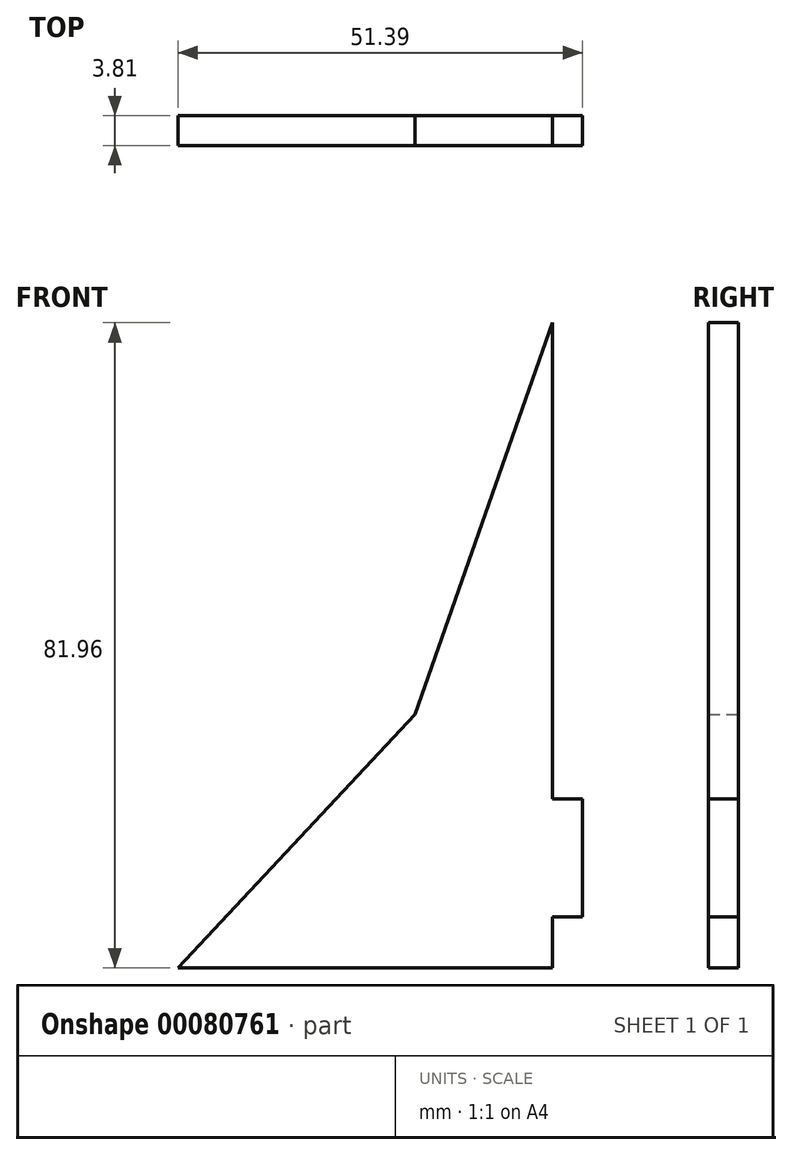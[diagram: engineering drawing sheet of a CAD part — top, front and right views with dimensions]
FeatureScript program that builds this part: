
annotation { "Feature Type Name" : "Feature", "Feature Type Description" : "" }
export const myFeature = defineFeature(function(context is Context, id is Id, definition is map)
    precondition{}
    {
        {
            var Q0;
            Q0=qCreatedBy(makeId("Front.planeOp"),FACE);
            var sketch = newSketch(context, id + "F0", { "sketchPlane" : qUnion([Q0])});
            skLineSegment(sketch, "E0", {"start": v(-0.6, 113.58) * mm, "end": v(-18.04, 63.84) * mm});
            skLineSegment(sketch, "E1", {"start": v(-18.04, 63.84) * mm, "end": v(-48.18, 31.62) * mm});
            skLineSegment(sketch, "E2", {"start": v(-48.18, 31.62) * mm, "end": v(-0.6, 31.62) * mm});
            skLineSegment(sketch, "E3", {"start": v(-0.6, 113.58) * mm, "end": v(-0.6, 31.62) * mm});
            skLineSegment(sketch, "E4", {"start": v(-0.6, 53.08) * mm, "end": v(3.2, 53.08) * mm});
            skLineSegment(sketch, "E5", {"start": v(3.2, 53.08) * mm, "end": v(3.2, 38.08) * mm});
            skLineSegment(sketch, "E6", {"start": v(3.2, 38.08) * mm, "end": v(-0.6, 38.08) * mm});
            skSolve(sketch);
        }
        {
            var Q0;
            {var subQ1=sQuery(id+"F0.wireOp",EDGE,"E0");Q0=makeQuery(id+"F0.imprint","IMPRINT",FACE,{"disambiguationData":[TD([[makeQuery(id+"F0.imprint","IMPRINT",EDGE,{"derivedFrom":subQ1}),1.0]])]});}
            var Q1;
            {var subQ0=sQuery(id+"F0.wireOp",EDGE,"E4");Q1=makeQuery(id+"F0.imprint","IMPRINT",FACE,{"disambiguationData":[TD([[makeQuery(id+"F0.imprint","IMPRINT",EDGE,{"derivedFrom":subQ0}),-1.0]])]});}
            extrude(context, id + "F1", {"entities" : qUnion([Q0, Q1]), "depth" : 3.8 * mm});
        }
    });
